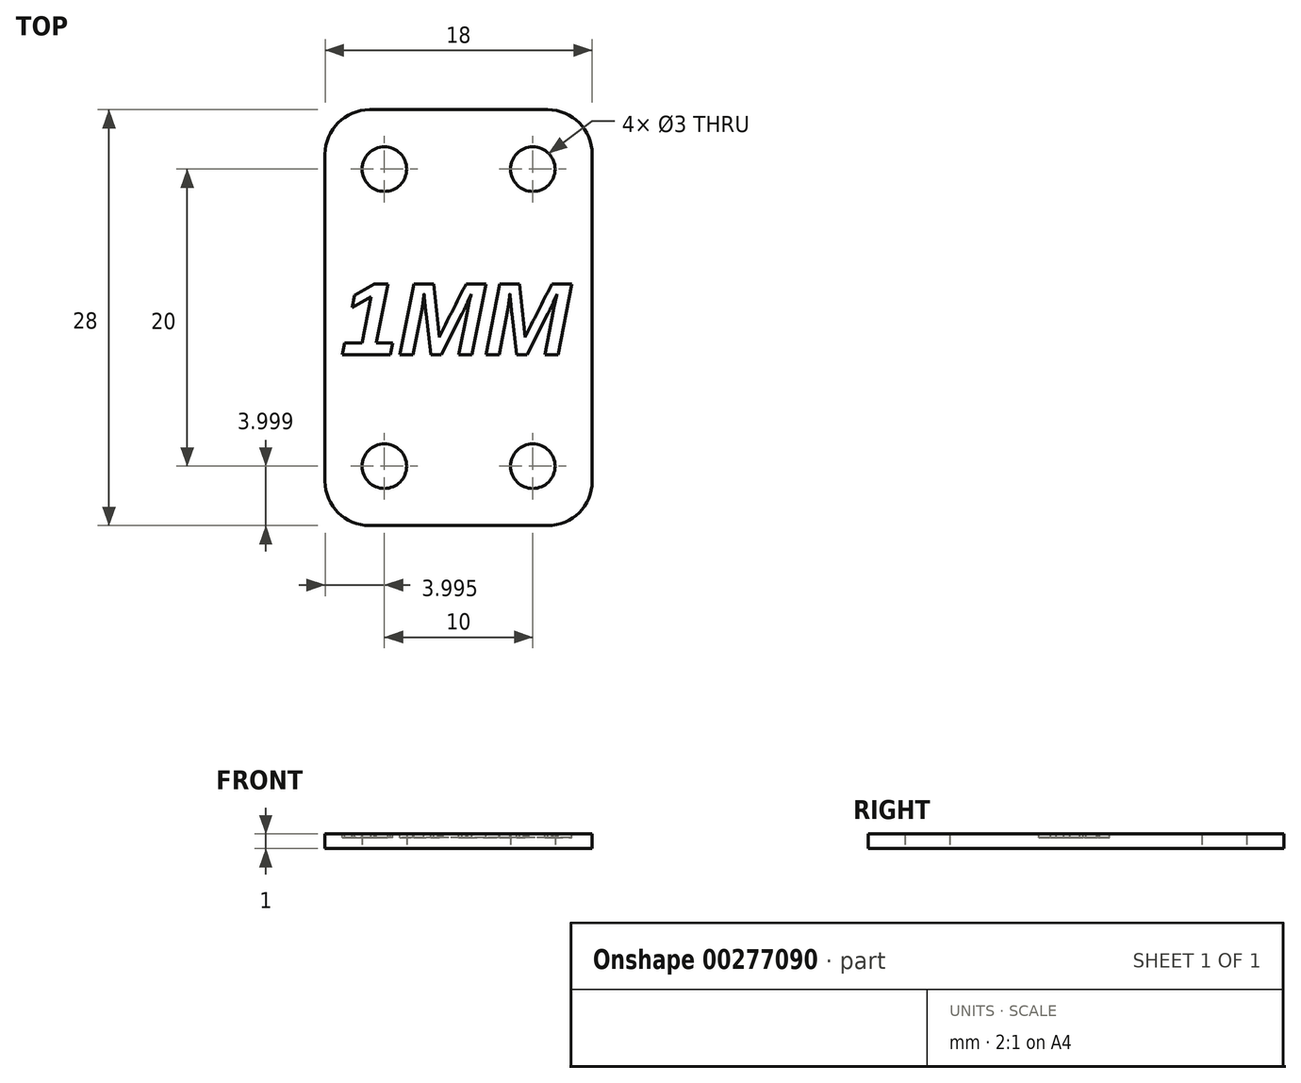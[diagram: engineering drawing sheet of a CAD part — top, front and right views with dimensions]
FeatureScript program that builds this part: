
annotation { "Feature Type Name" : "Feature", "Feature Type Description" : "" }
export const myFeature = defineFeature(function(context is Context, id is Id, definition is map)
    precondition{}
    {
        {
            var Q0;
            Q0=qCreatedBy(makeId("Top.planeOp"),FACE);
            var sketch = newSketch(context, id + "F0", { "sketchPlane" : qUnion([Q0])});
            skCircle(sketch, "E0", {"center": v(-51.93, 13.29) * mm, "radius": 1.5 * mm});
            skCircle(sketch, "E1", {"center": v(-41.93, 13.29) * mm, "radius": 1.5 * mm});
            skCircle(sketch, "E2", {"center": v(-41.93, -6.71) * mm, "radius": 1.5 * mm});
            skCircle(sketch, "E3", {"center": v(-51.93, -6.71) * mm, "radius": 1.5 * mm});
            skLineSegment(sketch, "E4.bottom", {"start": v(-55.93, -10.71) * mm, "end": v(-37.93, -10.71) * mm});
            skLineSegment(sketch, "E4.top", {"start": v(-55.93, 17.29) * mm, "end": v(-37.93, 17.29) * mm});
            skLineSegment(sketch, "E4.left", {"start": v(-55.93, -10.71) * mm, "end": v(-55.93, 17.29) * mm});
            skLineSegment(sketch, "E4.right", {"start": v(-37.93, -10.71) * mm, "end": v(-37.93, 17.29) * mm});
            skSolve(sketch);
        }
        {
            var Q0;
            Q0 = qSketchRegion(id + "F0", true);
            extrude(context, id + "F1", {"entities" : qUnion([Q0]), "depth" : 1 * mm, "offsetDistance" : 25 * mm});
        }
        {
            var Q0;
            Q0=makeQuery(id+"F1.opExtrude","SWEPT_EDGE",EDGE,{"disambiguationData":[OSD([sQuery(id+"F0.wireOp",EDGE,"E4.bottom"),sQuery(id+"F0.wireOp",EDGE,"E4.right")])]});
            var Q1;
            Q1=makeQuery(id+"F1.opExtrude","SWEPT_EDGE",EDGE,{"disambiguationData":[OSD([sQuery(id+"F0.wireOp",EDGE,"E4.top"),sQuery(id+"F0.wireOp",EDGE,"E4.right")])]});
            var Q2;
            Q2=makeQuery(id+"F1.opExtrude","SWEPT_EDGE",EDGE,{"disambiguationData":[OSD([sQuery(id+"F0.wireOp",EDGE,"E4.top"),sQuery(id+"F0.wireOp",EDGE,"E4.left")])]});
            var Q3;
            Q3=makeQuery(id+"F1.opExtrude","SWEPT_EDGE",EDGE,{"disambiguationData":[OSD([sQuery(id+"F0.wireOp",EDGE,"E4.bottom"),sQuery(id+"F0.wireOp",EDGE,"E4.left")])]});
            fillet(context, id + "F2", {"entities" : qUnion([Q0, Q1, Q2, Q3]), "radius" : 3 * mm, "tangentPropagation" : true, "allowEdgeOverflow" : false});
        }
        {
            var Q0;
            Q0=makeQuery(id+"F1.opExtrude","CAP_FACE",FACE,{"disambiguationData":[OSD([sQuery(id+"F0.wireOp",EDGE,"E0"),sQuery(id+"F0.wireOp",EDGE,"E1"),sQuery(id+"F0.wireOp",EDGE,"E2"),sQuery(id+"F0.wireOp",EDGE,"E3"),sQuery(id+"F0.wireOp",EDGE,"E4.bottom"),sQuery(id+"F0.wireOp",EDGE,"E4.top"),sQuery(id+"F0.wireOp",EDGE,"E4.left"),sQuery(id+"F0.wireOp",EDGE,"E4.right")])],"isStart":false});
            var sketch = newSketch(context, id + "F3", { "sketchPlane" : qUnion([Q0])});
            skText(sketch, "E5", { "text": "1MM", "fontName": "Arimo-BoldItalic.ttf"});
            const initialGuessF3  = {"E5": [-0.05487, 0.00079, 1, 0, 0.005]};
            skSetInitialGuess(sketch, initialGuessF3);
            skSolve(sketch);
        }
        {
            var Q0;
            Q0 = qSketchRegion(id + "F3", true);
            extrude(context, id + "F4", {"entities" : qUnion([Q0]), "operationType" : NewBodyOperationType.REMOVE, "oppositeDirection" : true, "depth" : .25 * mm, "offsetDistance" : 25 * mm});
        }
    });
